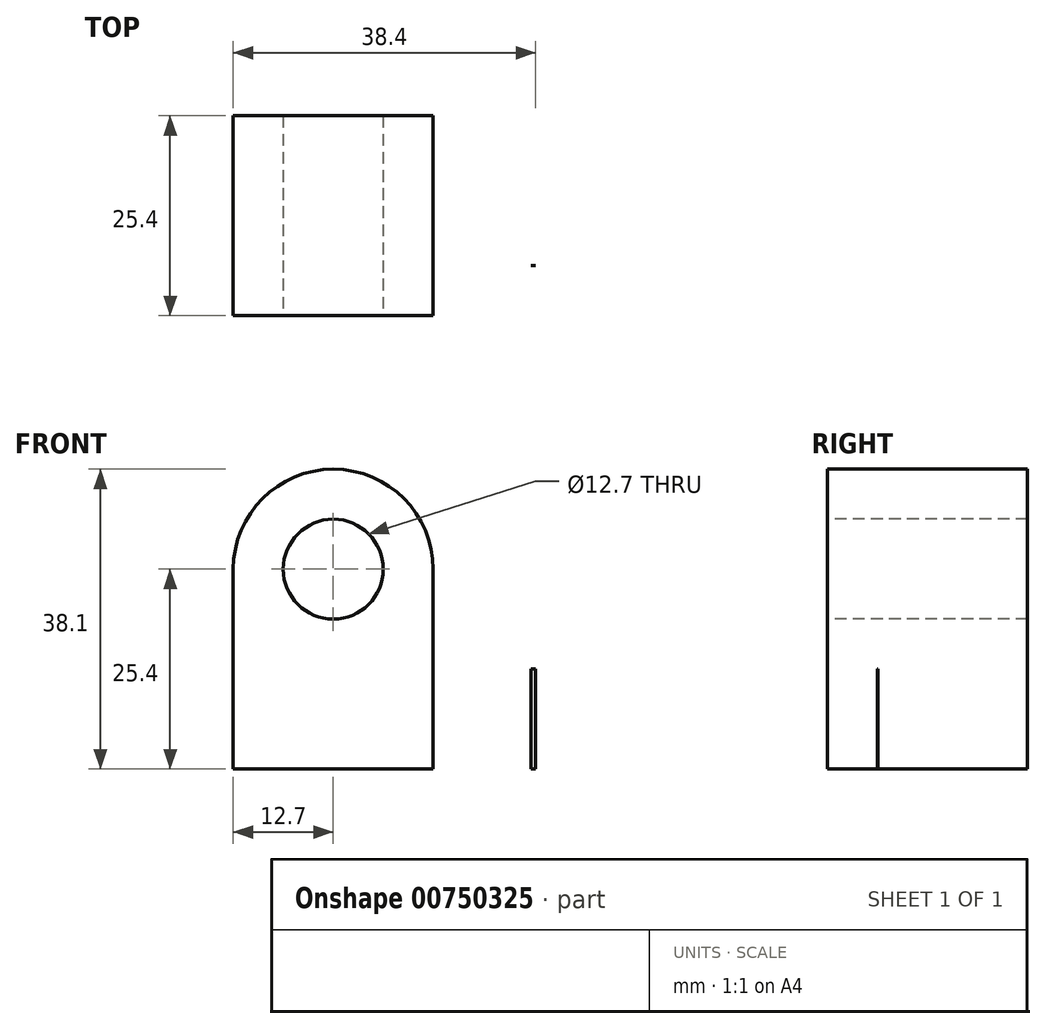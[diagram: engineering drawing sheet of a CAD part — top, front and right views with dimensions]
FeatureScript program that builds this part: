
annotation { "Feature Type Name" : "Feature", "Feature Type Description" : "" }
export const myFeature = defineFeature(function(context is Context, id is Id, definition is map)
    precondition{}
    {
        {
            var Q0;
            Q0=qCreatedBy(makeId("Front.planeOp"),FACE);
            var sketch = newSketch(context, id + "F0", { "sketchPlane" : qUnion([Q0])});
            skLineSegment(sketch, "E0", {"start": v(0, 0) * mm, "end": v(63.5, 0) * mm});
            skLineSegment(sketch, "E1", {"start": v(63.5, 0) * mm, "end": v(63.5, 12.7) * mm});
            skLineSegment(sketch, "E2", {"start": v(63.5, 12.7) * mm, "end": v(25.4, 12.7) * mm});
            skLineSegment(sketch, "E3", {"start": v(25.4, 12.7) * mm, "end": v(25.4, 38.1) * mm});
            skLineSegment(sketch, "E4", {"start": v(25.4, 38.1) * mm, "end": v(0, 38.1) * mm});
            skLineSegment(sketch, "E5", {"start": v(0, 38.1) * mm, "end": v(0, 0) * mm});
            skSolve(sketch);
        }
        {
            var Q0;
            Q0=makeQuery(id+"F0.imprint","IMPRINT",FACE,{"disambiguationData":[TD([[makeQuery(id+"F0.imprint","IMPRINT",EDGE,{"derivedFrom":sQuery(id+"F0.wireOp",EDGE,"E0")}),1.0]])]});
            extrude(context, id + "F1", {"entities" : qUnion([Q0]), "depth" : 25.4 * mm, "offsetDistance" : 25.4 * mm});
        }
        {
            var Q0;
            Q0=makeQuery(id+"F1.opExtrude","CAP_EDGE",EDGE,{"disambiguationData":[OSD([sQuery(id+"F0.wireOp",EDGE,"E1")])],"isStart":false});
            fillet(context, id + "F2", {"entities" : qUnion([Q0]), "radius" : 12.7 * mm, "tangentPropagation" : true, "allowEdgeOverflow" : false});
        }
        {
            var Q0;
            Q0=makeQuery(id+"F1.opExtrude","CAP_EDGE",EDGE,{"disambiguationData":[OSD([sQuery(id+"F0.wireOp",EDGE,"E1")])],"isStart":true});
            fillet(context, id + "F3", {"entities" : qUnion([Q0]), "radius" : 12.7 * mm, "tangentPropagation" : true, "allowEdgeOverflow" : false});
        }
        {
            var Q0;
            Q0=makeQuery(id+"F1.opExtrude","SWEPT_EDGE",EDGE,{"disambiguationData":[OSD([sQuery(id+"F0.wireOp",EDGE,"E3"),sQuery(id+"F0.wireOp",EDGE,"E4")])]});
            fillet(context, id + "F4", {"entities" : qUnion([Q0]), "radius" : 12.7 * mm, "tangentPropagation" : true, "allowEdgeOverflow" : false});
        }
        {
            var Q0;
            Q0=makeQuery(id+"F1.opExtrude","SWEPT_EDGE",EDGE,{"disambiguationData":[OSD([sQuery(id+"F0.wireOp",EDGE,"E4"),sQuery(id+"F0.wireOp",EDGE,"E5")])]});
            fillet(context, id + "F5", {"entities" : qUnion([Q0]), "radius" : 12.7 * mm, "tangentPropagation" : true, "allowEdgeOverflow" : false});
        }
        {
            var Q0;
            Q0=makeQuery(id+"F1.opExtrude","SWEPT_FACE",FACE,{"disambiguationData":[OSD([sQuery(id+"F0.wireOp",EDGE,"E2")])]});
            var sketch = newSketch(context, id + "F6", { "sketchPlane" : qUnion([Q0])});
            skCircle(sketch, "E6", {"center": v(38.1, -12.7) * mm, "radius": 6.35 * mm});
            skCircle(sketch, "E7", {"center": v(50.8, -12.7) * mm, "radius": 6.35 * mm});
            skLineSegment(sketch, "E8", {"start": v(38.1, -6.35) * mm, "end": v(50.8, -6.35) * mm});
            skPoint(sketch, "E8.startSnap0", {"position": v(38.1, 0) * mm});
            skLineSegment(sketch, "E9", {"start": v(37.8, -19.04) * mm, "end": v(50.8, -19.05) * mm});
            skSolve(sketch);
        }
        {
            var Q0;
            {var subQ0=sQuery(id+"F6.wireOp",EDGE,"E8");var subQ1=sQuery(id+"F6.wireOp",EDGE,"E6");var subQ2=makeQuery(id+"F6.imprint","INTERSECT",VERTEX,{"disambiguationData":[OD(0.0)],"derivedFrom":[subQ1,subQ0]});Q0=makeQuery(id+"F6.imprint","IMPRINT",FACE,{"disambiguationData":[TD([[makeQuery(id+"F6.imprint","IMPRINT",EDGE,{"disambiguationData":[TD([[subQ2,1.0]])],"derivedFrom":subQ1}),1.0]])]});}
            var Q1;
            {var subQ0=sQuery(id+"F6.wireOp",EDGE,"E9");var subQ1=sQuery(id+"F6.wireOp",EDGE,"E6");var subQ2=makeQuery(id+"F6.imprint","INTERSECT",VERTEX,{"disambiguationData":[OD(0.0)],"derivedFrom":[subQ1,subQ0]});Q1=makeQuery(id+"F6.imprint","IMPRINT",FACE,{"disambiguationData":[TD([[makeQuery(id+"F6.imprint","IMPRINT",EDGE,{"disambiguationData":[TD([[subQ2,-1.0]])],"derivedFrom":subQ1}),1.0]])]});}
            var Q2;
            {var subQ0=sQuery(id+"F6.wireOp",EDGE,"E8");var subQ1=sQuery(id+"F6.wireOp",EDGE,"E6");var subQ2=makeQuery(id+"F6.imprint","INTERSECT",VERTEX,{"disambiguationData":[OD(1.0)],"derivedFrom":[subQ1,subQ0]});Q2=makeQuery(id+"F6.imprint","IMPRINT",FACE,{"disambiguationData":[TD([[makeQuery(id+"F6.imprint","IMPRINT",EDGE,{"disambiguationData":[TD([[subQ2,1.0]])],"derivedFrom":subQ1}),-1.0]])]});}
            var Q3;
            {var subQ0=sQuery(id+"F6.wireOp",EDGE,"E9");var subQ1=sQuery(id+"F6.wireOp",EDGE,"E6");var subQ2=makeQuery(id+"F6.imprint","INTERSECT",VERTEX,{"disambiguationData":[OD(1.0)],"derivedFrom":[subQ1,subQ0]});Q3=makeQuery(id+"F6.imprint","IMPRINT",FACE,{"disambiguationData":[TD([[makeQuery(id+"F6.imprint","IMPRINT",EDGE,{"disambiguationData":[TD([[subQ2,-1.0]])],"derivedFrom":subQ1}),-1.0]])]});}
            var Q4;
            {var subQ1=sQuery(id+"F6.wireOp",EDGE,"E6");var subQ6=sQuery(id+"F6.wireOp",EDGE,"E8");var subQ9=makeQuery(id+"F6.imprint","INTERSECT",VERTEX,{"disambiguationData":[OD(1.0)],"derivedFrom":[subQ1,subQ6]});Q4=makeQuery(id+"F6.imprint","IMPRINT",FACE,{"disambiguationData":[TD([[makeQuery(id+"F6.imprint","IMPRINT",EDGE,{"disambiguationData":[TD([[subQ9,1.0]])],"derivedFrom":subQ1}),1.0]])]});}
            var Q5;
            {var subQ0=sQuery(id+"F6.wireOp",EDGE,"E7");var subQ1=sQuery(id+"F6.wireOp",EDGE,"E6");var subQ2=makeQuery(id+"F6.imprint","INTERSECT",VERTEX,{"disambiguationData":[OD(0.0)],"derivedFrom":[subQ1,subQ0]});Q5=makeQuery(id+"F6.imprint","IMPRINT",FACE,{"disambiguationData":[TD([[makeQuery(id+"F6.imprint","IMPRINT",EDGE,{"disambiguationData":[TD([[subQ2,1.0]])],"derivedFrom":subQ1}),-1.0]])]});}
            var Q6;
            {var subQ0=sQuery(id+"F6.wireOp",EDGE,"E7");var subQ1=sQuery(id+"F6.wireOp",EDGE,"E6");var subQ2=makeQuery(id+"F6.imprint","INTERSECT",VERTEX,{"disambiguationData":[OD(0.0)],"derivedFrom":[subQ1,subQ0]});Q6=makeQuery(id+"F6.imprint","IMPRINT",FACE,{"disambiguationData":[TD([[makeQuery(id+"F6.imprint","IMPRINT",EDGE,{"disambiguationData":[TD([[subQ2,1.0]])],"derivedFrom":subQ1}),1.0]])]});}
            var Q7;
            {var subQ0=sQuery(id+"F6.wireOp",EDGE,"E7");var subQ1=makeQuery(id+"F6.imprint","INTERSECT",VERTEX,{"derivedFrom":[subQ0,sQuery(id+"F6.wireOp",EDGE,"E8")]});Q7=makeQuery(id+"F6.imprint","IMPRINT",FACE,{"disambiguationData":[TD([[makeQuery(id+"F6.imprint","IMPRINT",EDGE,{"disambiguationData":[TD([[subQ1,-1.0]])],"derivedFrom":subQ0}),1.0]])]});}
            extrude(context, id + "F7", {"entities" : qUnion([Q0, Q1, Q2, Q3, Q4, Q5, Q6, Q7]), "operationType" : NewBodyOperationType.REMOVE, "oppositeDirection" : true, "depth" : 25.4 * mm, "offsetDistance" : 25.4 * mm});
        }
        {
            var Q0;
            Q0=makeQuery(id+"F1.opExtrude","CAP_FACE",FACE,{"disambiguationData":[OSD([sQuery(id+"F0.wireOp",EDGE,"E0"),sQuery(id+"F0.wireOp",EDGE,"E1"),sQuery(id+"F0.wireOp",EDGE,"E2"),sQuery(id+"F0.wireOp",EDGE,"E3"),sQuery(id+"F0.wireOp",EDGE,"E4"),sQuery(id+"F0.wireOp",EDGE,"E5")])],"isStart":false});
            var sketch = newSketch(context, id + "F8", { "sketchPlane" : qUnion([Q0])});
            skCircle(sketch, "E10", {"center": v(12.7, 25.4) * mm, "radius": 6.35 * mm});
            skSolve(sketch);
        }
        {
            var Q0;
            Q0=makeQuery(id+"F8.imprint","IMPRINT",FACE,{"disambiguationData":[TD([[makeQuery(id+"F8.imprint","IMPRINT",EDGE,{"derivedFrom":sQuery(id+"F8.wireOp",EDGE,"E10")}),1.0]])]});
            extrude(context, id + "F9", {"entities" : qUnion([Q0]), "operationType" : NewBodyOperationType.REMOVE, "oppositeDirection" : true, "depth" : 31.75 * mm, "offsetDistance" : 25.4 * mm});
        }
    });
